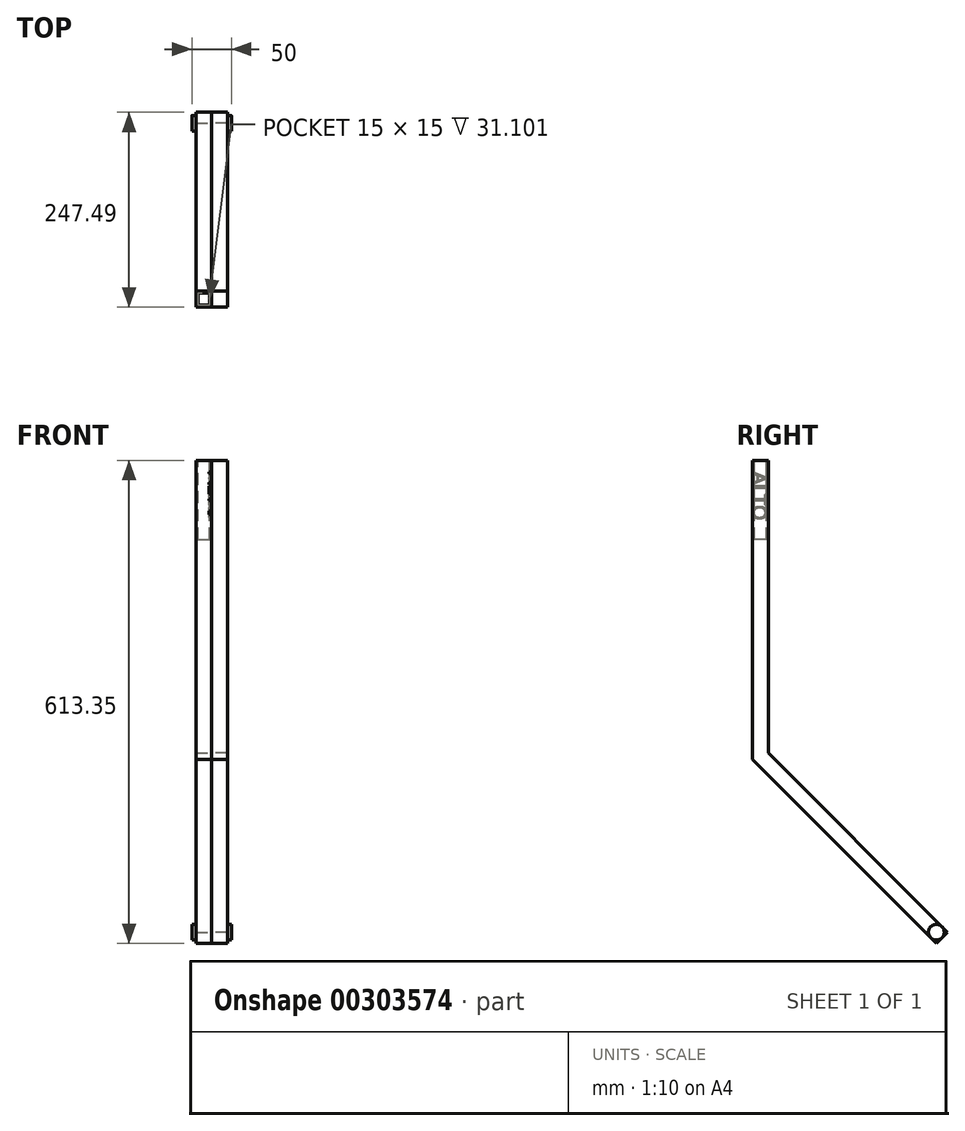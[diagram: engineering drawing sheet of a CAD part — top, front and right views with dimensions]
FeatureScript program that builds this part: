
annotation { "Feature Type Name" : "Feature", "Feature Type Description" : "" }
export const myFeature = defineFeature(function(context is Context, id is Id, definition is map)
    precondition{}
    {
        {
            var Q0;
            Q0=qCreatedBy(makeId("Right.planeOp"),FACE);
            var sketch = newSketch(context, id + "F0", { "sketchPlane" : qUnion([Q0])});
            skLineSegment(sketch, "E0.bottom", {"start": v(-73.87, 203.36) * mm, "end": v(-53.87, 203.36) * mm});
            skLineSegment(sketch, "E0.left", {"start": v(-73.87, 203.36) * mm, "end": v(-73.87, -176.64) * mm});
            skLineSegment(sketch, "E0.right", {"start": v(-53.87, 203.36) * mm, "end": v(-53.87, -168.36) * mm});
            skLineSegment(sketch, "E1", {"start": v(-53.87, -168.36) * mm, "end": v(173.62, -395.85) * mm});
            skLineSegment(sketch, "E2", {"start": v(173.62, -395.85) * mm, "end": v(159.48, -409.99) * mm});
            skLineSegment(sketch, "E3", {"start": v(159.48, -409.99) * mm, "end": v(-73.87, -176.64) * mm});
            skLineSegment(sketch, "E4", {"start": v(-147.1, -386.46) * mm, "end": v(66.8, -600.37) * mm, "construction": true});
            skLineSegment(sketch, "E5", {"start": v(-73.87, -176.64) * mm, "end": v(-53.87, -168.36) * mm});
            skSolve(sketch);
        }
        {
            var Q0;
            Q0=makeQuery(id+"F0.imprint","IMPRINT",FACE,{"disambiguationData":[TD([[makeQuery(id+"F0.imprint","IMPRINT",EDGE,{"derivedFrom":sQuery(id+"F0.wireOp",EDGE,"E0.bottom")}),-1.0]])]});
            var Q1;
            Q1=makeQuery(id+"F0.imprint","IMPRINT",FACE,{"disambiguationData":[TD([[makeQuery(id+"F0.imprint","IMPRINT",EDGE,{"derivedFrom":sQuery(id+"F0.wireOp",EDGE,"E1")}),-1.0]])]});
            extrude(context, id + "F1", {"entities" : qUnion([Q0, Q1]), "depth" : 20 * mm});
        }
        {
            var Q0;
            Q0=makeQuery(id+"F1.opExtrude","CAP_FACE",FACE,{"disambiguationData":[OSD([sQuery(id+"F0.wireOp",EDGE,"E0.bottom"),sQuery(id+"F0.wireOp",EDGE,"E0.left"),sQuery(id+"F0.wireOp",EDGE,"E0.right"),sQuery(id+"F0.wireOp",EDGE,"E1"),sQuery(id+"F0.wireOp",EDGE,"E2"),sQuery(id+"F0.wireOp",EDGE,"E3")])],"isStart":false});
            var sketch = newSketch(context, id + "F2", { "sketchPlane" : qUnion([Q0])});
            skLineSegment(sketch, "E6", {"start": v(159.48, -409.99) * mm, "end": v(159.48, -358.98) * mm, "construction": true});
            skLineSegment(sketch, "E7", {"start": v(173.62, -395.85) * mm, "end": v(101.05, -395.85) * mm, "construction": true});
            skCircle(sketch, "E8", {"center": v(159.48, -395.85) * mm, "radius": 10 * mm});
            skSolve(sketch);
        }
        {
            var Q0;
            {var subQ0=sQuery(id+"F2.wireOp",EDGE,"E8");var subQ1=makeQuery(id+"F2.imprint","INTERSECT",VERTEX,{"derivedFrom":[makeQuery(id+"F1.opExtrude","CAP_EDGE",EDGE,{"disambiguationData":[OSD([sQuery(id+"F0.wireOp",EDGE,"E3")])],"isStart":false}),subQ0]});Q0=makeQuery(id+"F2.imprint","IMPRINT",FACE,{"disambiguationData":[TD([[makeQuery(id+"F2.imprint","IMPRINT",EDGE,{"disambiguationData":[TD([[subQ1,1.0]])],"derivedFrom":subQ0}),1.0]])]});}
            extrude(context, id + "F3", {"entities" : qUnion([Q0]), "operationType" : NewBodyOperationType.ADD, "depth" : 5 * mm});
        }
        {
            var Q0;
            Q0=makeQuery(id+"F1.opExtrude","SWEPT_BODY",BODY,{"disambiguationData":[OSD([sQuery(id+"F0.wireOp",EDGE,"E0.bottom"),sQuery(id+"F0.wireOp",EDGE,"E0.left"),sQuery(id+"F0.wireOp",EDGE,"E0.right"),sQuery(id+"F0.wireOp",EDGE,"E1"),sQuery(id+"F0.wireOp",EDGE,"E2"),sQuery(id+"F0.wireOp",EDGE,"E3")])]});
            var Q1;
            Q1=qCreatedBy(makeId("Right.planeOp"),FACE);
            mirror(context, id + "F4", {"entities" : qUnion([Q0]), "mirrorPlane" : qUnion([Q1])});
        }
        {
            var Q0;
            Q0=makeQuery(id+"F4.opPattern","COPY",FACE,{"derivedFrom":makeQuery(id+"F1.opExtrude","SWEPT_FACE",FACE,{"disambiguationData":[OSD([sQuery(id+"F0.wireOp",EDGE,"E0.bottom")])]}),"instanceName":"1"});
            var sketch = newSketch(context, id + "F5", { "sketchPlane" : qUnion([Q0])});
            skLineSegment(sketch, "E9.bottom", {"start": v(-17.5, -56.37) * mm, "end": v(-2.5, -56.37) * mm});
            skLineSegment(sketch, "E9.top", {"start": v(-17.5, -71.37) * mm, "end": v(-2.5, -71.37) * mm});
            skLineSegment(sketch, "E9.left", {"start": v(-17.5, -56.37) * mm, "end": v(-17.5, -71.37) * mm});
            skLineSegment(sketch, "E9.right", {"start": v(-2.5, -56.37) * mm, "end": v(-2.5, -71.37) * mm});
            skPoint(sketch, "E9.middle", {"position": v(-10, -63.87) * mm});
            skPoint(sketch, "E9.middle.positionSnap0", {"position": v(0, -63.87) * mm});
            skPoint(sketch, "E9.middle.positionSnap1", {"position": v(-10, -53.87) * mm});
            skPoint(sketch, "E9.centerSnap0", {"position": v(0, -63.87) * mm});
            skPoint(sketch, "E9.centerSnap1", {"position": v(-10, -53.87) * mm});
            skSolve(sketch);
        }
        {
            var Q0;
            Q0=makeQuery(id+"F5.imprint","IMPRINT",FACE,{"disambiguationData":[TD([[makeQuery(id+"F5.imprint","IMPRINT",EDGE,{"derivedFrom":sQuery(id+"F5.wireOp",EDGE,"E9.bottom")}),-1.0]])]});
            extrude(context, id + "F6", {"entities" : qUnion([Q0]), "operationType" : NewBodyOperationType.REMOVE, "oppositeDirection" : true, "depth" : 100 * mm});
        }
        {
            var Q0;
            Q0=makeQuery(id+"F4.opPattern","COPY",FACE,{"derivedFrom":makeQuery(id+"F1.opExtrude","CAP_FACE",FACE,{"disambiguationData":[OSD([sQuery(id+"F0.wireOp",EDGE,"E0.bottom"),sQuery(id+"F0.wireOp",EDGE,"E0.left"),sQuery(id+"F0.wireOp",EDGE,"E0.right"),sQuery(id+"F0.wireOp",EDGE,"E1"),sQuery(id+"F0.wireOp",EDGE,"E2"),sQuery(id+"F0.wireOp",EDGE,"E3")])],"isStart":true}),"instanceName":"1"});
            var sketch = newSketch(context, id + "F7", { "sketchPlane" : qUnion([Q0])});
            skText(sketch, "E10", { "text": "ALTO", "fontName": "OpenSans-Regular.ttf"});
            const initialGuessF7  = {"E10": [-0.07387, 0.1888, 0, -1, 0.01774]};
            skSetInitialGuess(sketch, initialGuessF7);
            skSolve(sketch);
        }
        {
            var Q0;
            Q0 = qSketchRegion(id + "F7", true);
            extrude(context, id + "F8", {"entities" : qUnion([Q0]), "operationType" : NewBodyOperationType.REMOVE, "oppositeDirection" : true, "depth" : 3 * mm});
        }
    });
